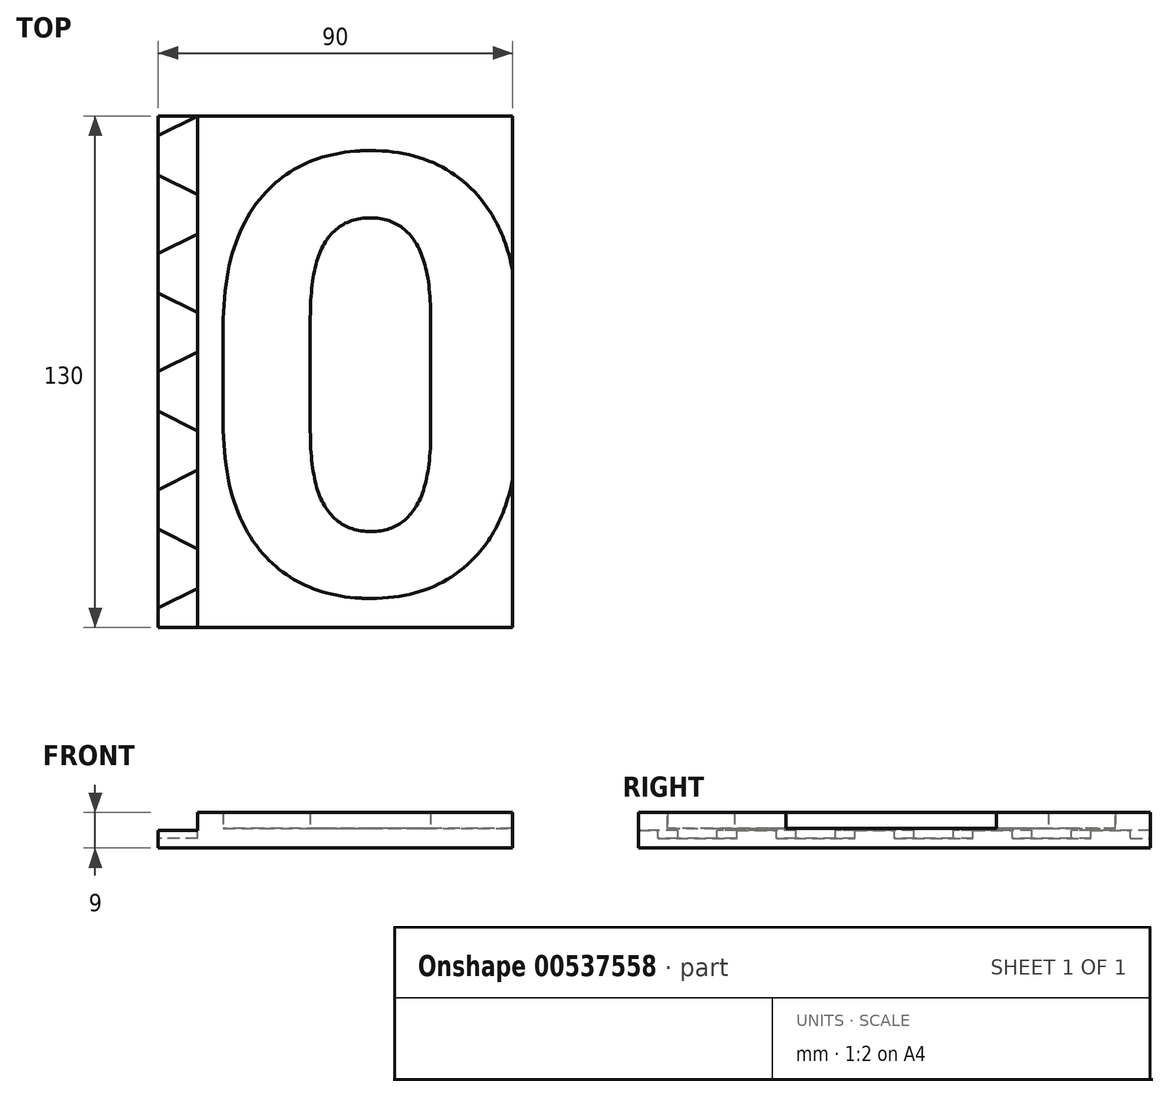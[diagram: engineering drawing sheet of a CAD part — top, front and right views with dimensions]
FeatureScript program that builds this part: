
annotation { "Feature Type Name" : "Feature", "Feature Type Description" : "" }
export const myFeature = defineFeature(function(context is Context, id is Id, definition is map)
    precondition{}
    {
        {
            var Q0;
            Q0=qCreatedBy(makeId("Top.planeOp"),FACE);
            var sketch = newSketch(context, id + "F0", { "sketchPlane" : qUnion([Q0])});
            skLineSegment(sketch, "E0.bottom", {"start": v(45, -65) * mm, "end": v(-45, -65) * mm});
            skLineSegment(sketch, "E0.top", {"start": v(45, 65) * mm, "end": v(-45, 65) * mm});
            skLineSegment(sketch, "E0.left", {"start": v(45, -65) * mm, "end": v(45, 65) * mm});
            skLineSegment(sketch, "E0.right", {"start": v(-45, -65) * mm, "end": v(-45, 65) * mm});
            skPoint(sketch, "E0.middle", {"position": v(0, 0) * mm});
            skSolve(sketch);
        }
        {
            var Q0;
            Q0 = qSketchRegion(id + "F0", true);
            extrude(context, id + "F1", {"entities" : qUnion([Q0]), "depth" : 5 * mm, "offsetDistance" : 25 * mm});
        }
        {
            var Q0;
            Q0=makeQuery(id+"F1.opExtrude","CAP_FACE",FACE,{"disambiguationData":[OSD([sQuery(id+"F0.wireOp",EDGE,"E0.bottom"),sQuery(id+"F0.wireOp",EDGE,"E0.top"),sQuery(id+"F0.wireOp",EDGE,"E0.left"),sQuery(id+"F0.wireOp",EDGE,"E0.right")])],"isStart":false});
            var sketch = newSketch(context, id + "F2", { "sketchPlane" : qUnion([Q0])});
            skLineSegment(sketch, "E1.bottom", {"start": v(45, 65) * mm, "end": v(-35, 65) * mm});
            skLineSegment(sketch, "E1.top", {"start": v(45, -65) * mm, "end": v(-35, -65) * mm});
            skLineSegment(sketch, "E1.left", {"start": v(45, 65) * mm, "end": v(45, -65) * mm});
            skLineSegment(sketch, "E1.right", {"start": v(-35, 65) * mm, "end": v(-35, -65) * mm});
            skText(sketch, "E2", { "text": "0", "fontName": "RobotoSlab-Bold.ttf"});
            skPoint(sketch, "E3", {"position": v(5, 65) * mm});
            skLineSegment(sketch, "E4", {"start": v(5, 65) * mm, "end": v(5, 56) * mm});
            skLineSegment(sketch, "E5", {"start": v(5, -56) * mm, "end": v(5, -65) * mm});
            const initialGuessF2  = {"E2": [-0.03585, -0.056, 1, 0, 0.112]};
            skSetInitialGuess(sketch, initialGuessF2);
            skSolve(sketch);
        }
        {
            var Q0;
            {var subQ2=sQuery(id+"F2.wireOp",EDGE,"E1.right");Q0=makeQuery(id+"F2.imprint","IMPRINT",FACE,{"disambiguationData":[TD([[makeQuery(id+"F2.imprint","IMPRINT",EDGE,{"derivedFrom":subQ2}),1.0]])]});}
            var Q1;
            Q1=makeQuery(id+"F2.imprint","IMPRINT",FACE,{"disambiguationData":[TD([[makeQuery(id+"F2.imprint","IMPRINT",EDGE,{"derivedFrom":sQuery(id+"F2.wireOp",EDGE,"E2.sketch_text.stroke-10")}),1.0]])]});
            var Q2;
            {var subQ6=sQuery(id+"F2.wireOp",EDGE,"E1.left");Q2=makeQuery(id+"F2.imprint","IMPRINT",FACE,{"disambiguationData":[TD([[makeQuery(id+"F2.imprint","IMPRINT",EDGE,{"derivedFrom":subQ6}),1.0]])]});}
            extrude(context, id + "F3", {"entities" : qUnion([Q0, Q1, Q2]), "operationType" : NewBodyOperationType.ADD, "depth" : 4 * mm, "offsetDistance" : 25 * mm});
        }
        {
            var Q0;
            {var subQ0=sQuery(id+"F0.wireOp",EDGE,"E0.top");var subQ1=sQuery(id+"F0.wireOp",EDGE,"E0.right");var subQ2=sQuery(id+"F0.wireOp",EDGE,"E0.bottom");Q0=makeQuery(id+"F3.boolean.opBoolean","SPLIT",FACE,{"disambiguationData":[TD([makeQuery(id+"F1.opExtrude","SWEPT_FACE",FACE,{"disambiguationData":[OSD([subQ2])]})])],"derivedFrom":makeQuery(id+"F1.opExtrude","CAP_FACE",FACE,{"disambiguationData":[OSD([subQ2,subQ0,sQuery(id+"F0.wireOp",EDGE,"E0.left"),subQ1])],"isStart":false})});}
            var sketch = newSketch(context, id + "F4", { "sketchPlane" : qUnion([Q0])});
            skLineSegment(sketch, "E6", {"start": v(-35, 65) * mm, "end": v(-45, 60) * mm});
            skLineSegment(sketch, "E7", {"start": v(-45, 60) * mm, "end": v(-45, 50) * mm});
            skLineSegment(sketch, "E8", {"start": v(-45, 50) * mm, "end": v(-35, 45) * mm});
            skLineSegment(sketch, "E9", {"start": v(-35, 65) * mm, "end": v(-35, 45) * mm});
            skLineSegment(sketch, "E10.0.1.0", {"start": v(-35, 35) * mm, "end": v(-45, 30) * mm});
            skLineSegment(sketch, "E10.0.1.1", {"start": v(-35, 35) * mm, "end": v(-35, 15) * mm});
            skLineSegment(sketch, "E10.0.1.2", {"start": v(-45, 30) * mm, "end": v(-45, 20) * mm});
            skLineSegment(sketch, "E10.0.1.3", {"start": v(-45, 20) * mm, "end": v(-35, 15) * mm});
            skLineSegment(sketch, "E10.0.2.0", {"start": v(-35, 5) * mm, "end": v(-45, 0) * mm});
            skLineSegment(sketch, "E10.0.2.1", {"start": v(-35, 5) * mm, "end": v(-35, -15) * mm});
            skLineSegment(sketch, "E10.0.2.2", {"start": v(-45, 0) * mm, "end": v(-45, -10) * mm});
            skLineSegment(sketch, "E10.0.2.3", {"start": v(-45, -10) * mm, "end": v(-35, -15) * mm});
            skLineSegment(sketch, "E10.0.3.0", {"start": v(-35, -25) * mm, "end": v(-45, -30) * mm});
            skLineSegment(sketch, "E10.0.3.1", {"start": v(-35, -25) * mm, "end": v(-35, -45) * mm});
            skLineSegment(sketch, "E10.0.3.2", {"start": v(-45, -30) * mm, "end": v(-45, -40) * mm});
            skLineSegment(sketch, "E10.0.3.3", {"start": v(-45, -40) * mm, "end": v(-35, -45) * mm});
            skLineSegment(sketch, "E10.0.4.0", {"start": v(-35, -55) * mm, "end": v(-45, -60) * mm});
            skLineSegment(sketch, "E10.0.4.1", {"start": v(-35, -55) * mm, "end": v(-35, -75) * mm});
            skLineSegment(sketch, "E10.0.4.2", {"start": v(-45, -60) * mm, "end": v(-45, -70) * mm});
            skLineSegment(sketch, "E10.0.4.3", {"start": v(-45, -70) * mm, "end": v(-35, -75) * mm});
            skLineSegment(sketch, "E10.direction1", {"start": v(-45, 60) * mm, "end": v(-25, 60) * mm, "construction": true});
            skLineSegment(sketch, "E10.direction2", {"start": v(-45, 60) * mm, "end": v(-45, 30) * mm, "construction": true});
            skLineSegment(sketch, "E11", {"start": v(-45, -65) * mm, "end": v(-35, -65) * mm});
            skSolve(sketch);
        }
        {
            var Q0;
            {var subQ0=sQuery(id+"F0.wireOp",EDGE,"E0.right");var subQ3=sQuery(id+"F0.wireOp",EDGE,"E0.top");var subQ4=makeQuery(id+"F1.opExtrude","SWEPT_FACE",FACE,{"disambiguationData":[OSD([subQ3])]});var subQ5=sQuery(id+"F0.wireOp",EDGE,"E0.bottom");Q0=makeQuery(id+"FFtWK41tFf5ku9X_1.boolean.opBoolean","SPLIT",FACE,{"disambiguationData":[TD([subQ4])],"derivedFrom":makeQuery(id+"F3.boolean.opBoolean","SPLIT",FACE,{"disambiguationData":[TD([makeQuery(id+"F1.opExtrude","SWEPT_FACE",FACE,{"disambiguationData":[OSD([subQ5])]})])],"derivedFrom":makeQuery(id+"F1.opExtrude","CAP_FACE",FACE,{"disambiguationData":[OSD([subQ5,subQ3,sQuery(id+"F0.wireOp",EDGE,"E0.left"),subQ0])],"isStart":false})})});}
            var Q1;
            {var subQ1=sQuery(id+"F0.wireOp",EDGE,"E0.right");var subQ3=sQuery(id+"F0.wireOp",EDGE,"E0.top");var subQ4=sQuery(id+"F0.wireOp",EDGE,"E0.bottom");Q1=makeQuery(id+"FFtWK41tFf5ku9X_1.boolean.opBoolean","SPLIT",FACE,{"disambiguationData":[TD([makeQuery(id+"FFtWK41tFf5ku9X_1.opExtrude","SWEPT_FACE",FACE,{"disambiguationData":[OSD([sQuery(id+"F4.wireOp",EDGE,"E8")])]})])],"derivedFrom":makeQuery(id+"F3.boolean.opBoolean","SPLIT",FACE,{"disambiguationData":[TD([makeQuery(id+"F1.opExtrude","SWEPT_FACE",FACE,{"disambiguationData":[OSD([subQ4])]})])],"derivedFrom":makeQuery(id+"F1.opExtrude","CAP_FACE",FACE,{"disambiguationData":[OSD([subQ4,subQ3,sQuery(id+"F0.wireOp",EDGE,"E0.left"),subQ1])],"isStart":false})})});}
            var Q2;
            {var subQ0=sQuery(id+"F0.wireOp",EDGE,"E0.right");var subQ3=sQuery(id+"F0.wireOp",EDGE,"E0.top");var subQ4=sQuery(id+"F0.wireOp",EDGE,"E0.bottom");Q2=makeQuery(id+"FFtWK41tFf5ku9X_1.boolean.opBoolean","SPLIT",FACE,{"disambiguationData":[TD([makeQuery(id+"FFtWK41tFf5ku9X_1.opExtrude","SWEPT_FACE",FACE,{"disambiguationData":[OSD([sQuery(id+"F4.wireOp",EDGE,"E10.0.1.3")])]})])],"derivedFrom":makeQuery(id+"F3.boolean.opBoolean","SPLIT",FACE,{"disambiguationData":[TD([makeQuery(id+"F1.opExtrude","SWEPT_FACE",FACE,{"disambiguationData":[OSD([subQ4])]})])],"derivedFrom":makeQuery(id+"F1.opExtrude","CAP_FACE",FACE,{"disambiguationData":[OSD([subQ4,subQ3,sQuery(id+"F0.wireOp",EDGE,"E0.left"),subQ0])],"isStart":false})})});}
            var Q3;
            {var subQ0=sQuery(id+"F0.wireOp",EDGE,"E0.right");var subQ3=sQuery(id+"F0.wireOp",EDGE,"E0.top");var subQ4=sQuery(id+"F0.wireOp",EDGE,"E0.bottom");Q3=makeQuery(id+"FFtWK41tFf5ku9X_1.boolean.opBoolean","SPLIT",FACE,{"disambiguationData":[TD([makeQuery(id+"FFtWK41tFf5ku9X_1.opExtrude","SWEPT_FACE",FACE,{"disambiguationData":[OSD([sQuery(id+"F4.wireOp",EDGE,"E10.0.2.3")])]})])],"derivedFrom":makeQuery(id+"F3.boolean.opBoolean","SPLIT",FACE,{"disambiguationData":[TD([makeQuery(id+"F1.opExtrude","SWEPT_FACE",FACE,{"disambiguationData":[OSD([subQ4])]})])],"derivedFrom":makeQuery(id+"F1.opExtrude","CAP_FACE",FACE,{"disambiguationData":[OSD([subQ4,subQ3,sQuery(id+"F0.wireOp",EDGE,"E0.left"),subQ0])],"isStart":false})})});}
            var Q4;
            {var subQ0=sQuery(id+"F0.wireOp",EDGE,"E0.right");var subQ3=sQuery(id+"F0.wireOp",EDGE,"E0.top");var subQ4=sQuery(id+"F0.wireOp",EDGE,"E0.bottom");Q4=makeQuery(id+"FFtWK41tFf5ku9X_1.boolean.opBoolean","SPLIT",FACE,{"disambiguationData":[TD([makeQuery(id+"FFtWK41tFf5ku9X_1.opExtrude","SWEPT_FACE",FACE,{"disambiguationData":[OSD([sQuery(id+"F4.wireOp",EDGE,"E10.0.3.3")])]})])],"derivedFrom":makeQuery(id+"F3.boolean.opBoolean","SPLIT",FACE,{"disambiguationData":[TD([makeQuery(id+"F1.opExtrude","SWEPT_FACE",FACE,{"disambiguationData":[OSD([subQ4])]})])],"derivedFrom":makeQuery(id+"F1.opExtrude","CAP_FACE",FACE,{"disambiguationData":[OSD([subQ4,subQ3,sQuery(id+"F0.wireOp",EDGE,"E0.left"),subQ0])],"isStart":false})})});}
            extrude(context, id + "F5", {"entities" : qUnion([Q0, Q1, Q2, Q3, Q4]), "operationType" : NewBodyOperationType.REMOVE, "oppositeDirection" : true, "depth" : 2.5 * mm, "offsetDistance" : 25 * mm});
        }
        {
            var Q0;
            Q0=makeQuery(id+"F4.imprint","IMPRINT",FACE,{"disambiguationData":[TD([[makeQuery(id+"F4.imprint","IMPRINT",EDGE,{"derivedFrom":sQuery(id+"F4.wireOp",EDGE,"E6")}),1.0]])]});
            var Q1;
            Q1=makeQuery(id+"F4.imprint","IMPRINT",FACE,{"disambiguationData":[TD([[makeQuery(id+"F4.imprint","IMPRINT",EDGE,{"derivedFrom":sQuery(id+"F4.wireOp",EDGE,"E10.0.1.0")}),1.0]])]});
            var Q2;
            Q2=makeQuery(id+"F4.imprint","IMPRINT",FACE,{"disambiguationData":[TD([[makeQuery(id+"F4.imprint","IMPRINT",EDGE,{"derivedFrom":sQuery(id+"F4.wireOp",EDGE,"E10.0.2.0")}),1.0]])]});
            var Q3;
            Q3=makeQuery(id+"F4.imprint","IMPRINT",FACE,{"disambiguationData":[TD([[makeQuery(id+"F4.imprint","IMPRINT",EDGE,{"derivedFrom":sQuery(id+"F4.wireOp",EDGE,"E10.0.3.0")}),1.0]])]});
            var Q4;
            {var subQ0=sQuery(id+"F4.wireOp",EDGE,"E10.0.4.0");Q4=makeQuery(id+"F4.imprint","IMPRINT",FACE,{"disambiguationData":[TD([[makeQuery(id+"F4.imprint","IMPRINT",EDGE,{"derivedFrom":subQ0}),1.0]])]});}
            extrude(context, id + "F6", {"entities" : qUnion([Q0, Q1, Q2, Q3, Q4]), "operationType" : NewBodyOperationType.ADD, "oppositeDirection" : true, "depth" : 4 * mm, "offsetDistance" : 25 * mm});
        }
        {
            var Q0;
            Q0=makeQuery(id+"F6.opExtrude","CAP_FACE",FACE,{"disambiguationData":[OSD([sQuery(id+"F4.wireOp",EDGE,"E6"),sQuery(id+"F4.wireOp",EDGE,"E7"),sQuery(id+"F4.wireOp",EDGE,"E8"),sQuery(id+"F4.wireOp",EDGE,"E9")])],"isStart":true});
            var Q1;
            Q1=makeQuery(id+"F6.opExtrude","CAP_FACE",FACE,{"disambiguationData":[OSD([sQuery(id+"F4.wireOp",EDGE,"E10.0.1.0"),sQuery(id+"F4.wireOp",EDGE,"E10.0.1.1"),sQuery(id+"F4.wireOp",EDGE,"E10.0.1.2"),sQuery(id+"F4.wireOp",EDGE,"E10.0.1.3")])],"isStart":true});
            var Q2;
            Q2=makeQuery(id+"F6.opExtrude","CAP_FACE",FACE,{"disambiguationData":[OSD([sQuery(id+"F4.wireOp",EDGE,"E10.0.2.0"),sQuery(id+"F4.wireOp",EDGE,"E10.0.2.1"),sQuery(id+"F4.wireOp",EDGE,"E10.0.2.2"),sQuery(id+"F4.wireOp",EDGE,"E10.0.2.3")])],"isStart":true});
            var Q3;
            Q3=makeQuery(id+"F6.opExtrude","CAP_FACE",FACE,{"disambiguationData":[OSD([sQuery(id+"F4.wireOp",EDGE,"E10.0.3.0"),sQuery(id+"F4.wireOp",EDGE,"E10.0.3.1"),sQuery(id+"F4.wireOp",EDGE,"E10.0.3.2"),sQuery(id+"F4.wireOp",EDGE,"E10.0.3.3")])],"isStart":true});
            var Q4;
            Q4=makeQuery(id+"F6.opExtrude","CAP_FACE",FACE,{"disambiguationData":[OSD([sQuery(id+"F4.wireOp",EDGE,"E10.0.4.0"),sQuery(id+"F4.wireOp",EDGE,"E10.0.4.1"),sQuery(id+"F4.wireOp",EDGE,"E10.0.4.2"),sQuery(id+"F4.wireOp",EDGE,"E11")])],"isStart":true});
            extrude(context, id + "F7", {"entities" : qUnion([Q0, Q1, Q2, Q3, Q4]), "operationType" : NewBodyOperationType.REMOVE, "oppositeDirection" : true, "depth" : 0.5 * mm, "offsetDistance" : 25 * mm});
        }
    });
